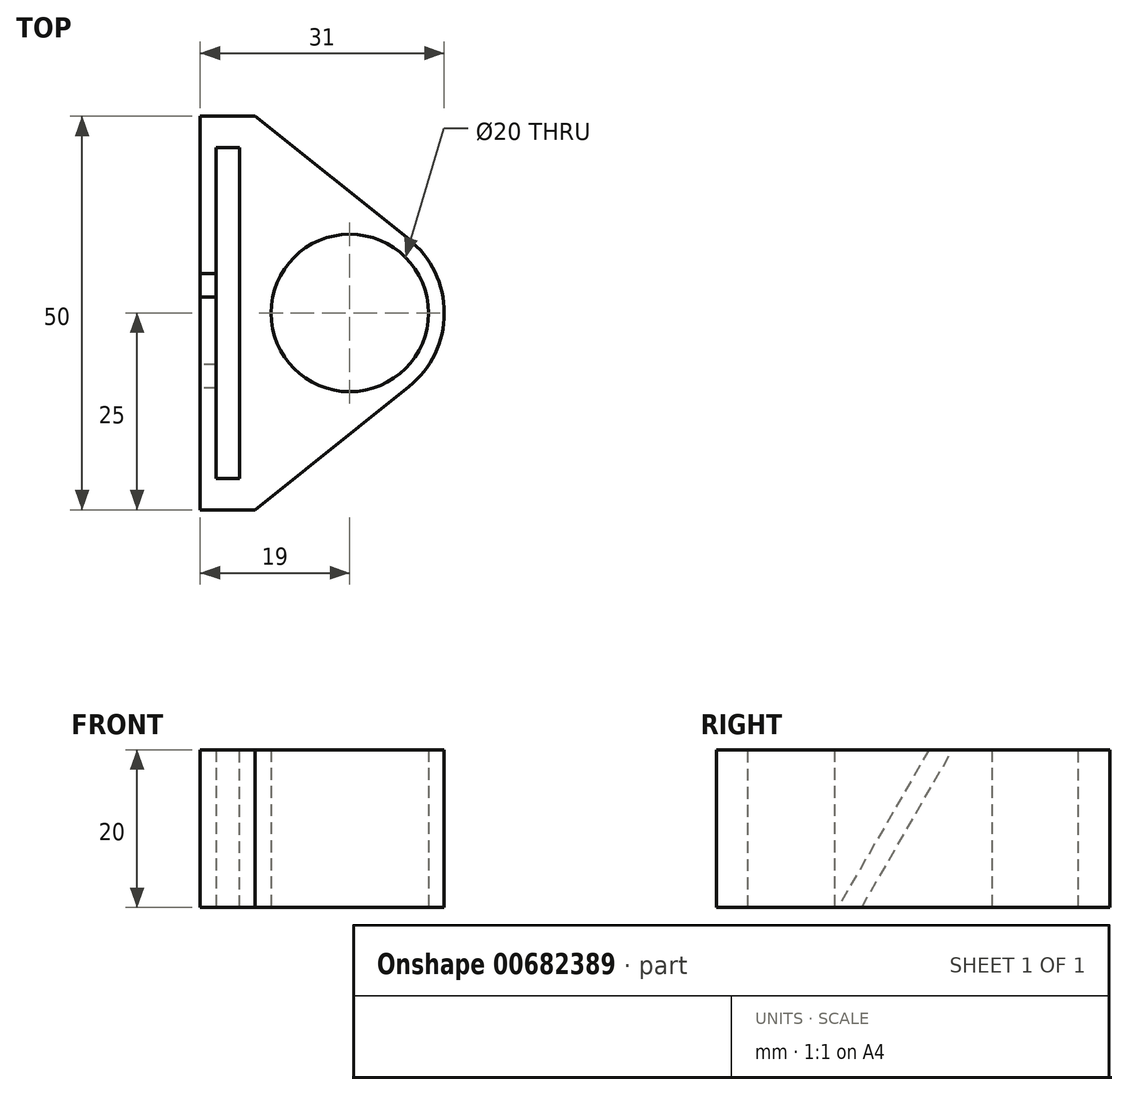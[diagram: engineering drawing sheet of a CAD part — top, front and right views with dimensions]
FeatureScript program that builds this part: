
annotation { "Feature Type Name" : "Feature", "Feature Type Description" : "" }
export const myFeature = defineFeature(function(context is Context, id is Id, definition is map)
    precondition{}
    {
        {
            var Q0;
            Q0=qCreatedBy(makeId("Top.planeOp"),FACE);
            var sketch = newSketch(context, id + "F0", { "sketchPlane" : qUnion([Q0])});
            skCircle(sketch, "E0", {"center": v(0, 0) * mm, "radius": 10 * mm});
            skCircle(sketch, "E1", {"center": v(0, 0) * mm, "radius": 12 * mm});
            skLineSegment(sketch, "E2", {"start": v(0, 0) * mm, "end": v(-22.33, 0) * mm, "construction": true});
            skLineSegment(sketch, "E3.MirrorCS", {"start": v(0, -15.38) * mm, "end": v(-12, -25) * mm});
            skLineSegment(sketch, "E4", {"start": v(-12, 0) * mm, "end": v(-12, 25) * mm});
            skLineSegment(sketch, "E5", {"start": v(-12, 25) * mm, "end": v(7.5, 9.36) * mm});
            skLineSegment(sketch, "E6.MirrorCS", {"start": v(-12, -25) * mm, "end": v(7.5, -9.36) * mm});
            skLineSegment(sketch, "E7.MirrorCS", {"start": v(-12, 0) * mm, "end": v(-12, -25) * mm});
            skSolve(sketch);
        }
        {
            var Q0;
            {var subQ0=sQuery(id+"F0.wireOp",EDGE,"E4");Q0=makeQuery(id+"F0.imprint","IMPRINT",FACE,{"disambiguationData":[TD([[makeQuery(id+"F0.imprint","IMPRINT",EDGE,{"derivedFrom":subQ0}),-1.0]])]});}
            var Q1;
            Q1=makeQuery(id+"F0.imprint","IMPRINT",FACE,{"disambiguationData":[TD([[makeQuery(id+"F0.imprint","IMPRINT",EDGE,{"derivedFrom":sQuery(id+"F0.wireOp",EDGE,"E0")}),-1.0]])]});
            var Q2;
            {var subQ0=sQuery(id+"F0.wireOp",EDGE,"E7.MirrorCS");Q2=makeQuery(id+"F0.imprint","IMPRINT",FACE,{"disambiguationData":[TD([[makeQuery(id+"F0.imprint","IMPRINT",EDGE,{"derivedFrom":subQ0}),1.0]])]});}
            extrude(context, id + "F1", {"entities" : qUnion([Q0, Q1, Q2]), "depth" : 20 * mm, "offsetDistance" : 25 * mm});
        }
        {
            var Q0;
            Q0=makeQuery(id+"F1.opExtrude","SWEPT_FACE",FACE,{"disambiguationData":[OSD([sQuery(id+"F0.wireOp",EDGE,"E4"),sQuery(id+"F0.wireOp",EDGE,"E7.MirrorCS")])]});
            extrude(context, id + "F2", {"entities" : qUnion([Q0]), "operationType" : NewBodyOperationType.ADD, "depth" : 7 * mm, "offsetDistance" : 25 * mm});
        }
        {
            var Q0;
            {var subQ0=sQuery(id+"F0.wireOp",EDGE,"E7.MirrorCS");var subQ1=sQuery(id+"F0.wireOp",EDGE,"E4");Q0=makeQuery(id+"F2.boolean.opBoolean","MERGE",FACE,{"derivedFrom":[makeQuery(id+"F1.opExtrude","CAP_FACE",FACE,{"disambiguationData":[OSD([sQuery(id+"F0.wireOp",EDGE,"E0"),sQuery(id+"F0.wireOp",EDGE,"E1"),subQ1,sQuery(id+"F0.wireOp",EDGE,"E5"),sQuery(id+"F0.wireOp",EDGE,"E6.MirrorCS"),subQ0])],"isStart":false}),makeQuery(id+"F2.opExtrude","SWEPT_FACE",FACE,{"disambiguationData":[OSD([subQ1,subQ0]),TDD([makeQuery(id+"F1.opExtrude","CAP_EDGE",EDGE,{"disambiguationData":[OSD([subQ1,subQ0])],"isStart":false})])]})]});}
            var sketch = newSketch(context, id + "F3", { "sketchPlane" : qUnion([Q0])});
            skLineSegment(sketch, "E8", {"start": v(-19, 0) * mm, "end": v(-10, 0) * mm, "construction": true});
            skLineSegment(sketch, "E9", {"start": v(-17, 21) * mm, "end": v(-17, -21) * mm});
            skPoint(sketch, "E10", {"position": v(-17, 0) * mm});
            skLineSegment(sketch, "E11", {"start": v(-14, 21) * mm, "end": v(-14, -21) * mm});
            skLineSegment(sketch, "E12", {"start": v(-17, -21) * mm, "end": v(-14, -21) * mm});
            skLineSegment(sketch, "E13", {"start": v(-17, 21) * mm, "end": v(-14, 21) * mm});
            skSolve(sketch);
        }
        {
            var Q0;
            Q0=makeQuery(id+"F3.imprint","IMPRINT",FACE,{"disambiguationData":[TD([[makeQuery(id+"F3.imprint","IMPRINT",EDGE,{"derivedFrom":sQuery(id+"F3.wireOp",EDGE,"E9")}),1.0]])]});
            extrude(context, id + "F4", {"entities" : qUnion([Q0]), "operationType" : NewBodyOperationType.REMOVE, "endBound" : BoundingType.THROUGH_ALL, "oppositeDirection" : true, "depth" : 25 * mm, "offsetDistance" : 25 * mm});
        }
        {
            var Q0;
            Q0=makeQuery(id+"F2.opExtrude","CAP_FACE",FACE,{"disambiguationData":[OSD([sQuery(id+"F0.wireOp",EDGE,"E4"),sQuery(id+"F0.wireOp",EDGE,"E7.MirrorCS")])],"isStart":false});
            var sketch = newSketch(context, id + "F5", { "sketchPlane" : qUnion([Q0])});
            skLineSegment(sketch, "E14", {"start": v(0, 20) * mm, "end": v(0, 0) * mm, "construction": true});
            skLineSegment(sketch, "E15", {"start": v(9.55, 0) * mm, "end": v(-2, 20) * mm});
            skLineSegment(sketch, "E16", {"start": v(6.55, 0) * mm, "end": v(-5, 20) * mm});
            skSolve(sketch);
        }
        {
            var Q0;
            {var subQ0=sQuery(id+"F5.wireOp",EDGE,"E15");Q0=makeQuery(id+"F5.imprint","IMPRINT",FACE,{"disambiguationData":[TD([[makeQuery(id+"F5.imprint","IMPRINT",EDGE,{"derivedFrom":subQ0}),1.0]])]});}
            var Q1;
            Q1=makeQuery(id+"F4.boolean.opBoolean","COPY",FACE,{"derivedFrom":makeQuery(id+"F4.opExtrude","SWEPT_FACE",FACE,{"disambiguationData":[OSD([sQuery(id+"F3.wireOp",EDGE,"E9")])]})});
            extrude(context, id + "F6", {"entities" : qUnion([Q0]), "operationType" : NewBodyOperationType.REMOVE, "endBound" : BoundingType.UP_TO_SURFACE, "oppositeDirection" : true, "depth" : 25 * mm, "endBoundEntityFace" : qUnion([Q1]), "offsetDistance" : 25 * mm});
        }
    });
